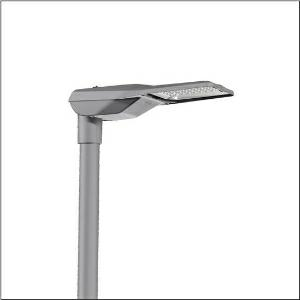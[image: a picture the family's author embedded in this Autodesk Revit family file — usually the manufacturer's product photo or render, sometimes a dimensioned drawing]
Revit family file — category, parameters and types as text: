
# Revit family: streetlight_sl_21_mini___p0_8a_5xe2u33s08hb_bff9
name_source: partatom
category: Lighting Fixtures
units: mm (PartAtom-declared; Revit-internal decimal feet)

## family parameters
Cut with Voids When Loaded = No
Host = Face
Light Source = No
Part Type = Normal
Room Calculation Point = No
Round Connector Dimension = Use Diameter
Shared = No

## types (1)
- --- (1 x LED, 9120 lm, 66 W, 3000K)
    Apparent Load = 66 VA
    CIE Flux Codes = 33 69 96 100 100
    Color Rendering = 70
    Color Temperature = 3000K
    Default Elevation = 1800 mm
    Description = Streetlight SL 21 mini, mast luminaire, primary light control with lens, of PMMA, primary optical cover: cover, of toughened safety glass, transparent, light distribution: P0.8a, light emission: direct distribution, primary light characteristic: asymmetric, installation type: post-top, side-entry, LED, High Power LED, rated luminous flux: 9.120lm, luminous efficacy: 138lm/W, light colour: 730, colour temperature: 3000K, control gear: D4i, control: pre-setting: logarithmic dimming characteristic, flexible luminous flux parameterisation, time-dependent luminous flux control, constant luminous flux control, overheat protection, mains connection: 220..240V, AC, 50/60Hz, start of lifetime: 66W, end of service life: 69W, reduction: 30W, luminaire housing, of diecast aluminium, powder-coated, SITECO metallic grey (DB 702S), corrosivity category C5 high according to DIN EN ISO 12944, multi-level sealing system, sealing non-destructively replaceable, inclination adjustable: 0°, 5°, 10°, 15°, please order mast flange separately, length: 628mm, width: 235mm, height: 110mm, mast flange for spigot size: 42mm (side-entry): 5XC10008XM4, 60/48mm (side-entry/post-top): 5XC10108XM2, 76/60mm (side-entry/post-top): 5XC10108XM1, mounting height: 4..8m, Smart Interface above, protection rating (complete): IP66, insulation class (complete): insulation class II (safety insulation), certification: CE, ENEC, ENEC+, VDE, impact resistance: IK10, permissible operating ambient temperature for outdoor applications: -40..+50°C, standard-compliant lighting for roads and squares, packaging unit: 1 piece

Light Distribution: P0.8a
    Height = 110 mm
    Lamp = 1 x LED
    Lamp Light Flux = 9120 lm
    Lamp Power = 66 W
    Lamp count = 1
    Length = 625 mm
    Luminous efficacy = 138 lm/W
    Manufacturer = Siteco
    ModVariant = No
    Model = 5XE2U33S08HB
    Number of Poles = 1
    OnlyDefault = Yes
    Power Factor = 1
    Product Name = Streetlight SL 21 mini | P0.8a
    Product group = mast luminaire | pylon top
    ProductGroupID = 6100
    Protection Class = Protection class II
    Protection Degree = IP 66
    RLX_Detail_Level = 1
    RLX_Emergency_Light_Flux = 0 lm
    RLX_Emergency_Type = 0
    RLX_Emergency_Type_DB = No
    RlxData = <blob elided: 91769 chars, md5=edf07bdb>
    Socket = socket
    Standby Power = 0 W
    System Light Flux = 9120 lm
    System Power = 66 W
    Type Comments = factory setting: luminous flux: 100 % | dim-lin: 254 | 670 mA
    Type Image = l_1003515.jpg
    URL = http://relux.com
    VarID = @adj_080255
    Voltage = 0 V
    Weight = 0.00 kg
    Width = 234 mm

## geometry (parser evidence)
native form markers: Blend x4, Sweep x10
no freeform markers — native parametric forms only
